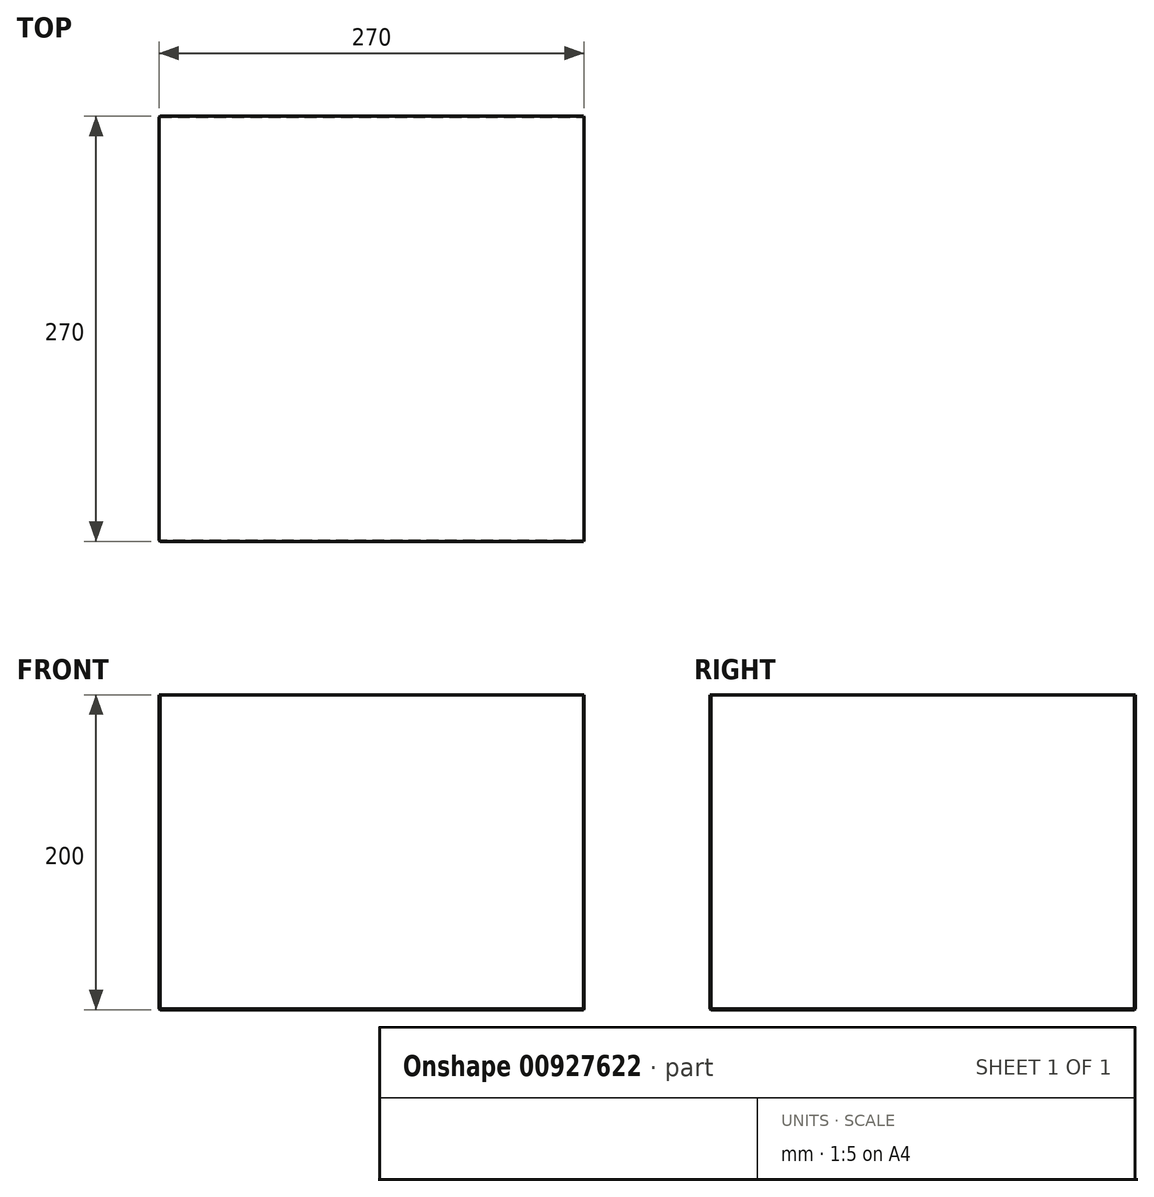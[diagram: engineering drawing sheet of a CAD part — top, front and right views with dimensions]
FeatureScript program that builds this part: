
annotation { "Feature Type Name" : "Feature", "Feature Type Description" : "" }
export const myFeature = defineFeature(function(context is Context, id is Id, definition is map)
    precondition{}
    {
        {
            var Q0;
            Q0=qCreatedBy(makeId("Front.planeOp"),FACE);
            var sketch = newSketch(context, id + "F0", { "sketchPlane" : qUnion([Q0])});
            skLineSegment(sketch, "E0.bottom", {"start": v(-270, 200) * mm, "end": v(0, 200) * mm});
            skLineSegment(sketch, "E0.top", {"start": v(-270, 0) * mm, "end": v(0, 0) * mm});
            skLineSegment(sketch, "E0.left", {"start": v(-270, 200) * mm, "end": v(-270, 0) * mm});
            skLineSegment(sketch, "E0.right", {"start": v(0, 200) * mm, "end": v(0, 0) * mm});
            skSolve(sketch);
        }
        {
            var Q0;
            Q0=makeQuery(id+"F0.imprint","IMPRINT",FACE,{"disambiguationData":[TD([[makeQuery(id+"F0.imprint","IMPRINT",EDGE,{"derivedFrom":sQuery(id+"F0.wireOp",EDGE,"E0.bottom")}),-1.0]])]});
            extrude(context, id + "F1", {"entities" : qUnion([Q0]), "oppositeDirection" : true, "depth" : 270 * mm, "offsetDistance" : 25 * mm});
        }
        {
            var Q0;
            Q0=makeQuery(id+"FSgalfFvMCT9fey_1.boolean.opBoolean","COPY",EDGE,{"derivedFrom":makeQuery(id+"FSgalfFvMCT9fey_1.opExtrude","CAP_EDGE",EDGE,{"disambiguationData":[OSD([sQuery(id+"FnhOHLOvYW450om_1.wireOp",EDGE,"d254c92e-775e-4ede-bdd0-727d0783bd5e0.MirrorCS")])],"isStart":true})});
            var Q1;
            Q1=makeQuery(id+"FSgalfFvMCT9fey_1.boolean.opBoolean","COPY",EDGE,{"derivedFrom":makeQuery(id+"FSgalfFvMCT9fey_1.opExtrude","CAP_EDGE",EDGE,{"disambiguationData":[OSD([sQuery(id+"FnhOHLOvYW450om_1.wireOp",EDGE,"SONESuy1-C7NP-j5df-jd7s-aXWFhhhByrCi")])],"isStart":true})});
            var Q2;
            Q2=makeQuery(id+"FSgalfFvMCT9fey_1.boolean.opBoolean","COPY",EDGE,{"derivedFrom":makeQuery(id+"FSgalfFvMCT9fey_1.opExtrude","CAP_EDGE",EDGE,{"disambiguationData":[OSD([sQuery(id+"FnhOHLOvYW450om_1.wireOp",EDGE,"yTDIKtbv-X4WC-F9KA-t1CG-33wgw8SEEBby")])],"isStart":true})});
            var Q3;
            Q3=makeQuery(id+"F1.opExtrude","CAP_EDGE",EDGE,{"disambiguationData":[OSD([sQuery(id+"F0.wireOp",EDGE,"E0.right")])],"isStart":true});
            var Q4;
            Q4=makeQuery(id+"F1.opExtrude","CAP_EDGE",EDGE,{"disambiguationData":[OSD([sQuery(id+"F0.wireOp",EDGE,"E0.right")])],"isStart":false});
            var Q5;
            Q5=makeQuery(id+"FSgalfFvMCT9fey_1.boolean.opBoolean","COPY",EDGE,{"derivedFrom":makeQuery(id+"FSgalfFvMCT9fey_1.opExtrude","CAP_EDGE",EDGE,{"disambiguationData":[OSD([sQuery(id+"FnhOHLOvYW450om_1.wireOp",EDGE,"lgSL1Au9-R2pw-915Y-fwfb-ga2PFbBGtXTd")])],"isStart":true})});
            var Q6;
            Q6=makeQuery(id+"F1m9xjpztgzHuyf_1.boolean.opBoolean","INTERSECT",EDGE,{"derivedFrom":[makeQuery(id+"F1.opExtrude","CAP_FACE",FACE,{"disambiguationData":[OSD([sQuery(id+"F0.wireOp",EDGE,"E0.bottom"),sQuery(id+"F0.wireOp",EDGE,"E0.top"),sQuery(id+"F0.wireOp",EDGE,"E0.left"),sQuery(id+"F0.wireOp",EDGE,"E0.right")])],"isStart":false}),makeQuery(id+"F1m9xjpztgzHuyf_1.opExtrude","SWEPT_FACE",FACE,{"disambiguationData":[OSD([sQuery(id+"FoSPC7aUubqrOsp_1.wireOp",EDGE,"V5KF5Hjf-UBSR-eE55-Q0oZ-NXqfqmdGQwhS")])]})]});
            var Q7;
            Q7=makeQuery(id+"FSgalfFvMCT9fey_1.boolean.opBoolean","INTERSECT",EDGE,{"derivedFrom":[makeQuery(id+"F1m9xjpztgzHuyf_1.boolean.opBoolean","COPY",FACE,{"derivedFrom":makeQuery(id+"F1m9xjpztgzHuyf_1.opExtrude","SWEPT_FACE",FACE,{"disambiguationData":[OSD([sQuery(id+"FoSPC7aUubqrOsp_1.wireOp",EDGE,"V5KF5Hjf-UBSR-eE55-Q0oZ-NXqfqmdGQwhS")])]})}),makeQuery(id+"FSgalfFvMCT9fey_1.opExtrude","SWEPT_FACE",FACE,{"disambiguationData":[OSD([sQuery(id+"FnhOHLOvYW450om_1.wireOp",EDGE,"lgSL1Au9-R2pw-915Y-fwfb-ga2PFbBGtXTd")])]})]});
            var Q8;
            Q8=makeQuery(id+"FSgalfFvMCT9fey_1.boolean.opBoolean","INTERSECT",EDGE,{"derivedFrom":[makeQuery(id+"F1m9xjpztgzHuyf_1.boolean.opBoolean","COPY",FACE,{"derivedFrom":makeQuery(id+"F1m9xjpztgzHuyf_1.opExtrude","SWEPT_FACE",FACE,{"disambiguationData":[OSD([sQuery(id+"FoSPC7aUubqrOsp_1.wireOp",EDGE,"V5KF5Hjf-UBSR-eE55-Q0oZ-NXqfqmdGQwhS")])]})}),makeQuery(id+"FSgalfFvMCT9fey_1.opExtrude","SWEPT_FACE",FACE,{"disambiguationData":[OSD([sQuery(id+"FnhOHLOvYW450om_1.wireOp",EDGE,"d254c92e-775e-4ede-bdd0-727d0783bd5e0.MirrorCS")])]})]});
            var Q9;
            Q9=makeQuery(id+"FSgalfFvMCT9fey_1.boolean.opBoolean","INTERSECT",EDGE,{"derivedFrom":[makeQuery(id+"F1m9xjpztgzHuyf_1.boolean.opBoolean","COPY",FACE,{"derivedFrom":makeQuery(id+"F1m9xjpztgzHuyf_1.opExtrude","SWEPT_FACE",FACE,{"disambiguationData":[OSD([sQuery(id+"FoSPC7aUubqrOsp_1.wireOp",EDGE,"V5KF5Hjf-UBSR-eE55-Q0oZ-NXqfqmdGQwhS")])]})}),makeQuery(id+"FSgalfFvMCT9fey_1.opExtrude","SWEPT_FACE",FACE,{"disambiguationData":[OSD([sQuery(id+"FnhOHLOvYW450om_1.wireOp",EDGE,"SONESuy1-C7NP-j5df-jd7s-aXWFhhhByrCi")])]})]});
            var Q10;
            Q10=makeQuery(id+"FSgalfFvMCT9fey_1.boolean.opBoolean","INTERSECT",EDGE,{"derivedFrom":[makeQuery(id+"F1m9xjpztgzHuyf_1.boolean.opBoolean","COPY",FACE,{"derivedFrom":makeQuery(id+"F1m9xjpztgzHuyf_1.opExtrude","SWEPT_FACE",FACE,{"disambiguationData":[OSD([sQuery(id+"FoSPC7aUubqrOsp_1.wireOp",EDGE,"V5KF5Hjf-UBSR-eE55-Q0oZ-NXqfqmdGQwhS")])]})}),makeQuery(id+"FSgalfFvMCT9fey_1.opExtrude","SWEPT_FACE",FACE,{"disambiguationData":[OSD([sQuery(id+"FnhOHLOvYW450om_1.wireOp",EDGE,"yTDIKtbv-X4WC-F9KA-t1CG-33wgw8SEEBby")])]})]});
            var Q11;
            Q11=makeQuery(id+"F1m9xjpztgzHuyf_1.boolean.opBoolean","COPY",EDGE,{"derivedFrom":makeQuery(id+"F1m9xjpztgzHuyf_1.opExtrude","CAP_EDGE",EDGE,{"disambiguationData":[OSD([sQuery(id+"FoSPC7aUubqrOsp_1.wireOp",EDGE,"V5KF5Hjf-UBSR-eE55-Q0oZ-NXqfqmdGQwhS")])],"isStart":true})});
            var Q12;
            Q12=makeQuery(id+"FSgalfFvMCT9fey_1.boolean.opBoolean","INTERSECT",EDGE,{"derivedFrom":[makeQuery(id+"F1m9xjpztgzHuyf_1.boolean.opBoolean","COPY",FACE,{"derivedFrom":makeQuery(id+"F1m9xjpztgzHuyf_1.opExtrude","SWEPT_FACE",FACE,{"disambiguationData":[OSD([sQuery(id+"FoSPC7aUubqrOsp_1.wireOp",EDGE,"d2c61c64-8efb-4917-b14a-e87310c20b8a.trimOffspring")])]})}),makeQuery(id+"FSgalfFvMCT9fey_1.opExtrude","SWEPT_FACE",FACE,{"disambiguationData":[OSD([sQuery(id+"FnhOHLOvYW450om_1.wireOp",EDGE,"yTDIKtbv-X4WC-F9KA-t1CG-33wgw8SEEBby")])]})]});
            var Q13;
            Q13=makeQuery(id+"FSgalfFvMCT9fey_1.boolean.opBoolean","INTERSECT",EDGE,{"derivedFrom":[makeQuery(id+"F1m9xjpztgzHuyf_1.boolean.opBoolean","COPY",FACE,{"derivedFrom":makeQuery(id+"F1m9xjpztgzHuyf_1.opExtrude","SWEPT_FACE",FACE,{"disambiguationData":[OSD([sQuery(id+"FoSPC7aUubqrOsp_1.wireOp",EDGE,"d1d635d0-32af-4d30-b4a8-8d9a20e03e98.trimOffspring")])]})}),makeQuery(id+"FSgalfFvMCT9fey_1.opExtrude","SWEPT_FACE",FACE,{"disambiguationData":[OSD([sQuery(id+"FnhOHLOvYW450om_1.wireOp",EDGE,"yTDIKtbv-X4WC-F9KA-t1CG-33wgw8SEEBby")])]})]});
            var Q14;
            Q14=makeQuery(id+"F1m9xjpztgzHuyf_1.boolean.opBoolean","COPY",EDGE,{"derivedFrom":makeQuery(id+"F1m9xjpztgzHuyf_1.opExtrude","CAP_EDGE",EDGE,{"disambiguationData":[OSD([sQuery(id+"FoSPC7aUubqrOsp_1.wireOp",EDGE,"d1d635d0-32af-4d30-b4a8-8d9a20e03e98.trimOffspring")])],"isStart":true})});
            var Q15;
            Q15=makeQuery(id+"F1m9xjpztgzHuyf_1.boolean.opBoolean","COPY",EDGE,{"derivedFrom":makeQuery(id+"F1m9xjpztgzHuyf_1.opExtrude","CAP_EDGE",EDGE,{"disambiguationData":[OSD([sQuery(id+"FoSPC7aUubqrOsp_1.wireOp",EDGE,"d2c61c64-8efb-4917-b14a-e87310c20b8a.trimOffspring")])],"isStart":true})});
            var Q16;
            Q16=makeQuery(id+"FSgalfFvMCT9fey_1.boolean.opBoolean","INTERSECT",EDGE,{"derivedFrom":[makeQuery(id+"F1m9xjpztgzHuyf_1.boolean.opBoolean","COPY",FACE,{"derivedFrom":makeQuery(id+"F1m9xjpztgzHuyf_1.opExtrude","SWEPT_FACE",FACE,{"disambiguationData":[OSD([sQuery(id+"FoSPC7aUubqrOsp_1.wireOp",EDGE,"d2c61c64-8efb-4917-b14a-e87310c20b8a.trimOffspring")])]})}),makeQuery(id+"FSgalfFvMCT9fey_1.opExtrude","SWEPT_FACE",FACE,{"disambiguationData":[OSD([sQuery(id+"FnhOHLOvYW450om_1.wireOp",EDGE,"SONESuy1-C7NP-j5df-jd7s-aXWFhhhByrCi")])]})]});
            var Q17;
            Q17=makeQuery(id+"FSgalfFvMCT9fey_1.boolean.opBoolean","INTERSECT",EDGE,{"derivedFrom":[makeQuery(id+"F1m9xjpztgzHuyf_1.boolean.opBoolean","COPY",FACE,{"derivedFrom":makeQuery(id+"F1m9xjpztgzHuyf_1.opExtrude","SWEPT_FACE",FACE,{"disambiguationData":[OSD([sQuery(id+"FoSPC7aUubqrOsp_1.wireOp",EDGE,"d2c61c64-8efb-4917-b14a-e87310c20b8a.trimOffspring")])]})}),makeQuery(id+"FSgalfFvMCT9fey_1.opExtrude","SWEPT_FACE",FACE,{"disambiguationData":[OSD([sQuery(id+"FnhOHLOvYW450om_1.wireOp",EDGE,"d254c92e-775e-4ede-bdd0-727d0783bd5e0.MirrorCS")])]})]});
            var Q18;
            Q18=makeQuery(id+"FSgalfFvMCT9fey_1.boolean.opBoolean","INTERSECT",EDGE,{"derivedFrom":[makeQuery(id+"F1m9xjpztgzHuyf_1.boolean.opBoolean","COPY",FACE,{"derivedFrom":makeQuery(id+"F1m9xjpztgzHuyf_1.opExtrude","SWEPT_FACE",FACE,{"disambiguationData":[OSD([sQuery(id+"FoSPC7aUubqrOsp_1.wireOp",EDGE,"d1d635d0-32af-4d30-b4a8-8d9a20e03e98.trimOffspring")])]})}),makeQuery(id+"FSgalfFvMCT9fey_1.opExtrude","SWEPT_FACE",FACE,{"disambiguationData":[OSD([sQuery(id+"FnhOHLOvYW450om_1.wireOp",EDGE,"d254c92e-775e-4ede-bdd0-727d0783bd5e0.MirrorCS")])]})]});
            var Q19;
            Q19=makeQuery(id+"FSgalfFvMCT9fey_1.boolean.opBoolean","INTERSECT",EDGE,{"derivedFrom":[makeQuery(id+"F1m9xjpztgzHuyf_1.boolean.opBoolean","COPY",FACE,{"derivedFrom":makeQuery(id+"F1m9xjpztgzHuyf_1.opExtrude","SWEPT_FACE",FACE,{"disambiguationData":[OSD([sQuery(id+"FoSPC7aUubqrOsp_1.wireOp",EDGE,"d1d635d0-32af-4d30-b4a8-8d9a20e03e98.trimOffspring")])]})}),makeQuery(id+"FSgalfFvMCT9fey_1.opExtrude","SWEPT_FACE",FACE,{"disambiguationData":[OSD([sQuery(id+"FnhOHLOvYW450om_1.wireOp",EDGE,"SONESuy1-C7NP-j5df-jd7s-aXWFhhhByrCi")])]})]});
            var Q20;
            Q20=makeQuery(id+"FSgalfFvMCT9fey_1.boolean.opBoolean","INTERSECT",EDGE,{"derivedFrom":[makeQuery(id+"F1m9xjpztgzHuyf_1.boolean.opBoolean","COPY",FACE,{"derivedFrom":makeQuery(id+"F1m9xjpztgzHuyf_1.opExtrude","SWEPT_FACE",FACE,{"disambiguationData":[OSD([sQuery(id+"FoSPC7aUubqrOsp_1.wireOp",EDGE,"d1d635d0-32af-4d30-b4a8-8d9a20e03e98.trimOffspring")])]})}),makeQuery(id+"FSgalfFvMCT9fey_1.opExtrude","SWEPT_FACE",FACE,{"disambiguationData":[OSD([sQuery(id+"FnhOHLOvYW450om_1.wireOp",EDGE,"lgSL1Au9-R2pw-915Y-fwfb-ga2PFbBGtXTd")])]})]});
            var Q21;
            Q21=makeQuery(id+"F1m9xjpztgzHuyf_1.boolean.opBoolean","INTERSECT",EDGE,{"derivedFrom":[makeQuery(id+"F1.opExtrude","CAP_FACE",FACE,{"disambiguationData":[OSD([sQuery(id+"F0.wireOp",EDGE,"E0.bottom"),sQuery(id+"F0.wireOp",EDGE,"E0.top"),sQuery(id+"F0.wireOp",EDGE,"E0.left"),sQuery(id+"F0.wireOp",EDGE,"E0.right")])],"isStart":false}),makeQuery(id+"F1m9xjpztgzHuyf_1.opExtrude","SWEPT_FACE",FACE,{"disambiguationData":[OSD([sQuery(id+"FoSPC7aUubqrOsp_1.wireOp",EDGE,"d1d635d0-32af-4d30-b4a8-8d9a20e03e98.trimOffspring")])]})]});
            var Q22;
            Q22=makeQuery(id+"F1m9xjpztgzHuyf_1.boolean.opBoolean","INTERSECT",EDGE,{"derivedFrom":[makeQuery(id+"F1.opExtrude","CAP_FACE",FACE,{"disambiguationData":[OSD([sQuery(id+"F0.wireOp",EDGE,"E0.bottom"),sQuery(id+"F0.wireOp",EDGE,"E0.top"),sQuery(id+"F0.wireOp",EDGE,"E0.left"),sQuery(id+"F0.wireOp",EDGE,"E0.right")])],"isStart":false}),makeQuery(id+"F1m9xjpztgzHuyf_1.opExtrude","SWEPT_FACE",FACE,{"disambiguationData":[OSD([sQuery(id+"FoSPC7aUubqrOsp_1.wireOp",EDGE,"d2c61c64-8efb-4917-b14a-e87310c20b8a.trimOffspring")])]})]});
            var Q23;
            Q23=makeQuery(id+"FSgalfFvMCT9fey_1.boolean.opBoolean","INTERSECT",EDGE,{"derivedFrom":[makeQuery(id+"F1m9xjpztgzHuyf_1.boolean.opBoolean","COPY",FACE,{"derivedFrom":makeQuery(id+"F1m9xjpztgzHuyf_1.opExtrude","SWEPT_FACE",FACE,{"disambiguationData":[OSD([sQuery(id+"FoSPC7aUubqrOsp_1.wireOp",EDGE,"d2c61c64-8efb-4917-b14a-e87310c20b8a.trimOffspring")])]})}),makeQuery(id+"FSgalfFvMCT9fey_1.opExtrude","SWEPT_FACE",FACE,{"disambiguationData":[OSD([sQuery(id+"FnhOHLOvYW450om_1.wireOp",EDGE,"lgSL1Au9-R2pw-915Y-fwfb-ga2PFbBGtXTd")])]})]});
            var Q24;
            Q24=makeQuery(id+"FSgalfFvMCT9fey_1.boolean.opBoolean","INTERSECT",EDGE,{"derivedFrom":[makeQuery(id+"F1m9xjpztgzHuyf_1.boolean.opBoolean","COPY",FACE,{"derivedFrom":makeQuery(id+"F1m9xjpztgzHuyf_1.opExtrude","SWEPT_FACE",FACE,{"disambiguationData":[OSD([sQuery(id+"FoSPC7aUubqrOsp_1.wireOp",EDGE,"JywAzUny-DW4f-TQhj-XWJa-UNkQjx5q2ZEw")])]})}),makeQuery(id+"FSgalfFvMCT9fey_1.opExtrude","SWEPT_FACE",FACE,{"disambiguationData":[OSD([sQuery(id+"FnhOHLOvYW450om_1.wireOp",EDGE,"lgSL1Au9-R2pw-915Y-fwfb-ga2PFbBGtXTd")])]})]});
            var Q25;
            Q25=makeQuery(id+"F1m9xjpztgzHuyf_1.boolean.opBoolean","INTERSECT",EDGE,{"derivedFrom":[makeQuery(id+"F1.opExtrude","CAP_FACE",FACE,{"disambiguationData":[OSD([sQuery(id+"F0.wireOp",EDGE,"E0.bottom"),sQuery(id+"F0.wireOp",EDGE,"E0.top"),sQuery(id+"F0.wireOp",EDGE,"E0.left"),sQuery(id+"F0.wireOp",EDGE,"E0.right")])],"isStart":false}),makeQuery(id+"F1m9xjpztgzHuyf_1.opExtrude","SWEPT_FACE",FACE,{"disambiguationData":[OSD([sQuery(id+"FoSPC7aUubqrOsp_1.wireOp",EDGE,"JywAzUny-DW4f-TQhj-XWJa-UNkQjx5q2ZEw")])]})]});
            var Q26;
            Q26=makeQuery(id+"FSgalfFvMCT9fey_1.boolean.opBoolean","INTERSECT",EDGE,{"derivedFrom":[makeQuery(id+"F1m9xjpztgzHuyf_1.boolean.opBoolean","COPY",FACE,{"derivedFrom":makeQuery(id+"F1m9xjpztgzHuyf_1.opExtrude","SWEPT_FACE",FACE,{"disambiguationData":[OSD([sQuery(id+"FoSPC7aUubqrOsp_1.wireOp",EDGE,"JywAzUny-DW4f-TQhj-XWJa-UNkQjx5q2ZEw")])]})}),makeQuery(id+"FSgalfFvMCT9fey_1.opExtrude","SWEPT_FACE",FACE,{"disambiguationData":[OSD([sQuery(id+"FnhOHLOvYW450om_1.wireOp",EDGE,"d254c92e-775e-4ede-bdd0-727d0783bd5e0.MirrorCS")])]})]});
            var Q27;
            Q27=makeQuery(id+"FSgalfFvMCT9fey_1.boolean.opBoolean","INTERSECT",EDGE,{"derivedFrom":[makeQuery(id+"F1m9xjpztgzHuyf_1.boolean.opBoolean","COPY",FACE,{"derivedFrom":makeQuery(id+"F1m9xjpztgzHuyf_1.opExtrude","SWEPT_FACE",FACE,{"disambiguationData":[OSD([sQuery(id+"FoSPC7aUubqrOsp_1.wireOp",EDGE,"JywAzUny-DW4f-TQhj-XWJa-UNkQjx5q2ZEw")])]})}),makeQuery(id+"FSgalfFvMCT9fey_1.opExtrude","SWEPT_FACE",FACE,{"disambiguationData":[OSD([sQuery(id+"FnhOHLOvYW450om_1.wireOp",EDGE,"SONESuy1-C7NP-j5df-jd7s-aXWFhhhByrCi")])]})]});
            var Q28;
            Q28=makeQuery(id+"FSgalfFvMCT9fey_1.boolean.opBoolean","INTERSECT",EDGE,{"derivedFrom":[makeQuery(id+"F1m9xjpztgzHuyf_1.boolean.opBoolean","COPY",FACE,{"derivedFrom":makeQuery(id+"F1m9xjpztgzHuyf_1.opExtrude","SWEPT_FACE",FACE,{"disambiguationData":[OSD([sQuery(id+"FoSPC7aUubqrOsp_1.wireOp",EDGE,"JywAzUny-DW4f-TQhj-XWJa-UNkQjx5q2ZEw")])]})}),makeQuery(id+"FSgalfFvMCT9fey_1.opExtrude","SWEPT_FACE",FACE,{"disambiguationData":[OSD([sQuery(id+"FnhOHLOvYW450om_1.wireOp",EDGE,"yTDIKtbv-X4WC-F9KA-t1CG-33wgw8SEEBby")])]})]});
            var Q29;
            Q29=makeQuery(id+"F1m9xjpztgzHuyf_1.boolean.opBoolean","COPY",EDGE,{"derivedFrom":makeQuery(id+"F1m9xjpztgzHuyf_1.opExtrude","CAP_EDGE",EDGE,{"disambiguationData":[OSD([sQuery(id+"FoSPC7aUubqrOsp_1.wireOp",EDGE,"JywAzUny-DW4f-TQhj-XWJa-UNkQjx5q2ZEw")])],"isStart":true})});
            var Q30;
            Q30=makeQuery(id+"F1.opExtrude","CAP_EDGE",EDGE,{"disambiguationData":[OSD([sQuery(id+"F0.wireOp",EDGE,"E0.left")])],"isStart":true});
            var Q31;
            Q31=makeQuery(id+"FSgalfFvMCT9fey_1.boolean.opBoolean","INTERSECT",EDGE,{"derivedFrom":[makeQuery(id+"F1.opExtrude","SWEPT_FACE",FACE,{"disambiguationData":[OSD([sQuery(id+"F0.wireOp",EDGE,"E0.left")])]}),makeQuery(id+"FSgalfFvMCT9fey_1.opExtrude","SWEPT_FACE",FACE,{"disambiguationData":[OSD([sQuery(id+"FnhOHLOvYW450om_1.wireOp",EDGE,"yTDIKtbv-X4WC-F9KA-t1CG-33wgw8SEEBby")])]})]});
            var Q32;
            Q32=makeQuery(id+"FSgalfFvMCT9fey_1.boolean.opBoolean","INTERSECT",EDGE,{"derivedFrom":[makeQuery(id+"F1.opExtrude","SWEPT_FACE",FACE,{"disambiguationData":[OSD([sQuery(id+"F0.wireOp",EDGE,"E0.left")])]}),makeQuery(id+"FSgalfFvMCT9fey_1.opExtrude","SWEPT_FACE",FACE,{"disambiguationData":[OSD([sQuery(id+"FnhOHLOvYW450om_1.wireOp",EDGE,"SONESuy1-C7NP-j5df-jd7s-aXWFhhhByrCi")])]})]});
            var Q33;
            Q33=makeQuery(id+"FSgalfFvMCT9fey_1.boolean.opBoolean","INTERSECT",EDGE,{"derivedFrom":[makeQuery(id+"F1.opExtrude","SWEPT_FACE",FACE,{"disambiguationData":[OSD([sQuery(id+"F0.wireOp",EDGE,"E0.left")])]}),makeQuery(id+"FSgalfFvMCT9fey_1.opExtrude","SWEPT_FACE",FACE,{"disambiguationData":[OSD([sQuery(id+"FnhOHLOvYW450om_1.wireOp",EDGE,"d254c92e-775e-4ede-bdd0-727d0783bd5e0.MirrorCS")])]})]});
            var Q34;
            Q34=makeQuery(id+"FSgalfFvMCT9fey_1.boolean.opBoolean","INTERSECT",EDGE,{"derivedFrom":[makeQuery(id+"F1.opExtrude","SWEPT_FACE",FACE,{"disambiguationData":[OSD([sQuery(id+"F0.wireOp",EDGE,"E0.left")])]}),makeQuery(id+"FSgalfFvMCT9fey_1.opExtrude","SWEPT_FACE",FACE,{"disambiguationData":[OSD([sQuery(id+"FnhOHLOvYW450om_1.wireOp",EDGE,"lgSL1Au9-R2pw-915Y-fwfb-ga2PFbBGtXTd")])]})]});
            var Q35;
            Q35=makeQuery(id+"F1.opExtrude","CAP_EDGE",EDGE,{"disambiguationData":[OSD([sQuery(id+"F0.wireOp",EDGE,"E0.left")])],"isStart":false});
            var Q36;
            {var subQ0=sQuery(id+"FnhOHLOvYW450om_1.wireOp",EDGE,"WMZrNsfh-GP0r-MC8E-i3Dt-oq9u2fUcREUs");var subQ1=sQuery(id+"FoSPC7aUubqrOsp_1.wireOp",EDGE,"PDPpZB2r-T6CP-ZxPB-fvgC-Na7DPJPVDUVZ");Q36=makeQuery(id+"FSgalfFvMCT9fey_1.boolean.opBoolean","MERGE",FACE,{"derivedFrom":[makeQuery(id+"F1m9xjpztgzHuyf_1.boolean.opBoolean","COPY",FACE,{"derivedFrom":makeQuery(id+"F1m9xjpztgzHuyf_1.opExtrude","SWEPT_FACE",FACE,{"disambiguationData":[OSD([subQ1]),TDD([makeQuery(id+"FoSPC7aUubqrOsp_1.imprint","IMPRINT",EDGE,{"disambiguationData":[TD([[makeQuery(id+"FoSPC7aUubqrOsp_1.imprint","INTERSECT",VERTEX,{"derivedFrom":[sQuery(id+"FoSPC7aUubqrOsp_1.wireOp",EDGE,"JywAzUny-DW4f-TQhj-XWJa-UNkQjx5q2ZEw"),subQ1]}),-1.0]])],"derivedFrom":subQ1})])]})}),makeQuery(id+"F1m9xjpztgzHuyf_1.boolean.opBoolean","COPY",FACE,{"derivedFrom":makeQuery(id+"F1m9xjpztgzHuyf_1.opExtrude","SWEPT_FACE",FACE,{"disambiguationData":[OSD([subQ1]),TDD([makeQuery(id+"FoSPC7aUubqrOsp_1.imprint","IMPRINT",EDGE,{"disambiguationData":[TD([[makeQuery(id+"FoSPC7aUubqrOsp_1.imprint","INTERSECT",VERTEX,{"derivedFrom":[sQuery(id+"FoSPC7aUubqrOsp_1.wireOp",EDGE,"V5KF5Hjf-UBSR-eE55-Q0oZ-NXqfqmdGQwhS"),subQ1]}),1.0]])],"derivedFrom":subQ1})])]})})],"fromTools":[makeQuery(id+"FSgalfFvMCT9fey_1.opExtrude","SWEPT_FACE",FACE,{"disambiguationData":[OSD([subQ0]),TDD([makeQuery(id+"FnhOHLOvYW450om_1.imprint","IMPRINT",EDGE,{"disambiguationData":[TD([[makeQuery(id+"FnhOHLOvYW450om_1.imprint","INTERSECT",VERTEX,{"derivedFrom":[subQ0,sQuery(id+"FnhOHLOvYW450om_1.wireOp",EDGE,"SONESuy1-C7NP-j5df-jd7s-aXWFhhhByrCi")]}),1.0]])],"derivedFrom":subQ0})])]}),makeQuery(id+"FSgalfFvMCT9fey_1.opExtrude","SWEPT_FACE",FACE,{"disambiguationData":[OSD([subQ0]),TDD([makeQuery(id+"FnhOHLOvYW450om_1.imprint","IMPRINT",EDGE,{"disambiguationData":[TD([[makeQuery(id+"FnhOHLOvYW450om_1.imprint","INTERSECT",VERTEX,{"derivedFrom":[subQ0,sQuery(id+"FnhOHLOvYW450om_1.wireOp",EDGE,"lgSL1Au9-R2pw-915Y-fwfb-ga2PFbBGtXTd")]}),1.0]])],"derivedFrom":subQ0})])]})]});}
            var Q37;
            {var subQ0=sQuery(id+"F0.wireOp",EDGE,"E0.right");var subQ2=sQuery(id+"F0.wireOp",EDGE,"E0.top");var subQ5=makeQuery(id+"F1.opExtrude","SWEPT_FACE",FACE,{"disambiguationData":[OSD([subQ0])]});Q37=makeQuery(id+"FSgalfFvMCT9fey_1.boolean.opBoolean","SPLIT",FACE,{"disambiguationData":[TD([makeQuery(id+"FSgalfFvMCT9fey_1.opExtrude","SWEPT_FACE",FACE,{"disambiguationData":[OSD([sQuery(id+"FnhOHLOvYW450om_1.wireOp",EDGE,"yTDIKtbv-X4WC-F9KA-t1CG-33wgw8SEEBby")])]})])],"derivedFrom":makeQuery(id+"F1m9xjpztgzHuyf_1.boolean.opBoolean","SPLIT",FACE,{"disambiguationData":[TD([subQ5])],"derivedFrom":makeQuery(id+"F1.opExtrude","SWEPT_FACE",FACE,{"disambiguationData":[OSD([subQ2])]})})});}
            var Q38;
            {var subQ0=sQuery(id+"F0.wireOp",EDGE,"E0.right");var subQ1=makeQuery(id+"F1.opExtrude","SWEPT_FACE",FACE,{"disambiguationData":[OSD([subQ0])]});var subQ4=sQuery(id+"F0.wireOp",EDGE,"E0.top");Q38=makeQuery(id+"FSgalfFvMCT9fey_1.boolean.opBoolean","SPLIT",FACE,{"disambiguationData":[TD([makeQuery(id+"FSgalfFvMCT9fey_1.opExtrude","SWEPT_FACE",FACE,{"disambiguationData":[OSD([sQuery(id+"FnhOHLOvYW450om_1.wireOp",EDGE,"SONESuy1-C7NP-j5df-jd7s-aXWFhhhByrCi")])]})])],"derivedFrom":makeQuery(id+"F1m9xjpztgzHuyf_1.boolean.opBoolean","SPLIT",FACE,{"disambiguationData":[TD([subQ1])],"derivedFrom":makeQuery(id+"F1.opExtrude","SWEPT_FACE",FACE,{"disambiguationData":[OSD([subQ4])]})})});}
            var Q39;
            {var subQ0=sQuery(id+"F0.wireOp",EDGE,"E0.right");var subQ2=sQuery(id+"F0.wireOp",EDGE,"E0.top");var subQ5=makeQuery(id+"F1.opExtrude","SWEPT_FACE",FACE,{"disambiguationData":[OSD([subQ0])]});Q39=makeQuery(id+"FSgalfFvMCT9fey_1.boolean.opBoolean","SPLIT",FACE,{"disambiguationData":[TD([makeQuery(id+"FSgalfFvMCT9fey_1.opExtrude","SWEPT_FACE",FACE,{"disambiguationData":[OSD([sQuery(id+"FnhOHLOvYW450om_1.wireOp",EDGE,"lgSL1Au9-R2pw-915Y-fwfb-ga2PFbBGtXTd")])]})])],"derivedFrom":makeQuery(id+"F1m9xjpztgzHuyf_1.boolean.opBoolean","SPLIT",FACE,{"disambiguationData":[TD([subQ5])],"derivedFrom":makeQuery(id+"F1.opExtrude","SWEPT_FACE",FACE,{"disambiguationData":[OSD([subQ2])]})})});}
            var Q40;
            {var subQ2=sQuery(id+"F0.wireOp",EDGE,"E0.top");var subQ6=makeQuery(id+"F1m9xjpztgzHuyf_1.opExtrude","SWEPT_FACE",FACE,{"disambiguationData":[OSD([sQuery(id+"FoSPC7aUubqrOsp_1.wireOp",EDGE,"d1d635d0-32af-4d30-b4a8-8d9a20e03e98.trimOffspring")])]});Q40=makeQuery(id+"FSgalfFvMCT9fey_1.boolean.opBoolean","SPLIT",FACE,{"disambiguationData":[TD([makeQuery(id+"FSgalfFvMCT9fey_1.opExtrude","SWEPT_FACE",FACE,{"disambiguationData":[OSD([sQuery(id+"FnhOHLOvYW450om_1.wireOp",EDGE,"lgSL1Au9-R2pw-915Y-fwfb-ga2PFbBGtXTd")])]})])],"derivedFrom":makeQuery(id+"F1m9xjpztgzHuyf_1.boolean.opBoolean","SPLIT",FACE,{"disambiguationData":[TD([subQ6])],"derivedFrom":makeQuery(id+"F1.opExtrude","SWEPT_FACE",FACE,{"disambiguationData":[OSD([subQ2])]})})});}
            var Q41;
            {var subQ1=sQuery(id+"F0.wireOp",EDGE,"E0.left");var subQ2=sQuery(id+"F0.wireOp",EDGE,"E0.top");var subQ5=makeQuery(id+"F1.opExtrude","SWEPT_FACE",FACE,{"disambiguationData":[OSD([subQ1])]});Q41=makeQuery(id+"FSgalfFvMCT9fey_1.boolean.opBoolean","SPLIT",FACE,{"disambiguationData":[TD([makeQuery(id+"FSgalfFvMCT9fey_1.opExtrude","SWEPT_FACE",FACE,{"disambiguationData":[OSD([sQuery(id+"FnhOHLOvYW450om_1.wireOp",EDGE,"lgSL1Au9-R2pw-915Y-fwfb-ga2PFbBGtXTd")])]})])],"derivedFrom":makeQuery(id+"F1m9xjpztgzHuyf_1.boolean.opBoolean","SPLIT",FACE,{"disambiguationData":[TD([subQ5])],"derivedFrom":makeQuery(id+"F1.opExtrude","SWEPT_FACE",FACE,{"disambiguationData":[OSD([subQ2])]})})});}
            var Q42;
            {var subQ0=sQuery(id+"F0.wireOp",EDGE,"E0.left");var subQ1=makeQuery(id+"F1.opExtrude","SWEPT_FACE",FACE,{"disambiguationData":[OSD([subQ0])]});var subQ4=sQuery(id+"F0.wireOp",EDGE,"E0.top");Q42=makeQuery(id+"FSgalfFvMCT9fey_1.boolean.opBoolean","SPLIT",FACE,{"disambiguationData":[TD([makeQuery(id+"FSgalfFvMCT9fey_1.opExtrude","SWEPT_FACE",FACE,{"disambiguationData":[OSD([sQuery(id+"FnhOHLOvYW450om_1.wireOp",EDGE,"SONESuy1-C7NP-j5df-jd7s-aXWFhhhByrCi")])]})])],"derivedFrom":makeQuery(id+"F1m9xjpztgzHuyf_1.boolean.opBoolean","SPLIT",FACE,{"disambiguationData":[TD([subQ1])],"derivedFrom":makeQuery(id+"F1.opExtrude","SWEPT_FACE",FACE,{"disambiguationData":[OSD([subQ4])]})})});}
            var Q43;
            {var subQ1=sQuery(id+"F0.wireOp",EDGE,"E0.left");var subQ2=sQuery(id+"F0.wireOp",EDGE,"E0.top");var subQ5=makeQuery(id+"F1.opExtrude","SWEPT_FACE",FACE,{"disambiguationData":[OSD([subQ1])]});Q43=makeQuery(id+"FSgalfFvMCT9fey_1.boolean.opBoolean","SPLIT",FACE,{"disambiguationData":[TD([makeQuery(id+"FSgalfFvMCT9fey_1.opExtrude","SWEPT_FACE",FACE,{"disambiguationData":[OSD([sQuery(id+"FnhOHLOvYW450om_1.wireOp",EDGE,"yTDIKtbv-X4WC-F9KA-t1CG-33wgw8SEEBby")])]})])],"derivedFrom":makeQuery(id+"F1m9xjpztgzHuyf_1.boolean.opBoolean","SPLIT",FACE,{"disambiguationData":[TD([subQ5])],"derivedFrom":makeQuery(id+"F1.opExtrude","SWEPT_FACE",FACE,{"disambiguationData":[OSD([subQ2])]})})});}
            chamfer(context, id + "F2", {"entities" : qUnion([Q0, Q1, Q2, Q3, Q4, Q5, Q6, Q7, Q8, Q9, Q10, Q11, Q12, Q13, Q14, Q15, Q16, Q17, Q18, Q19, Q20, Q21, Q22, Q23, Q24, Q25, Q26, Q27, Q28, Q29, Q30, Q31, Q32, Q33, Q34, Q35, Q36, Q37, Q38, Q39, Q40, Q41, Q42, Q43]), "width" : 0.5 * mm, "tangentPropagation" : true});
        }
    });
